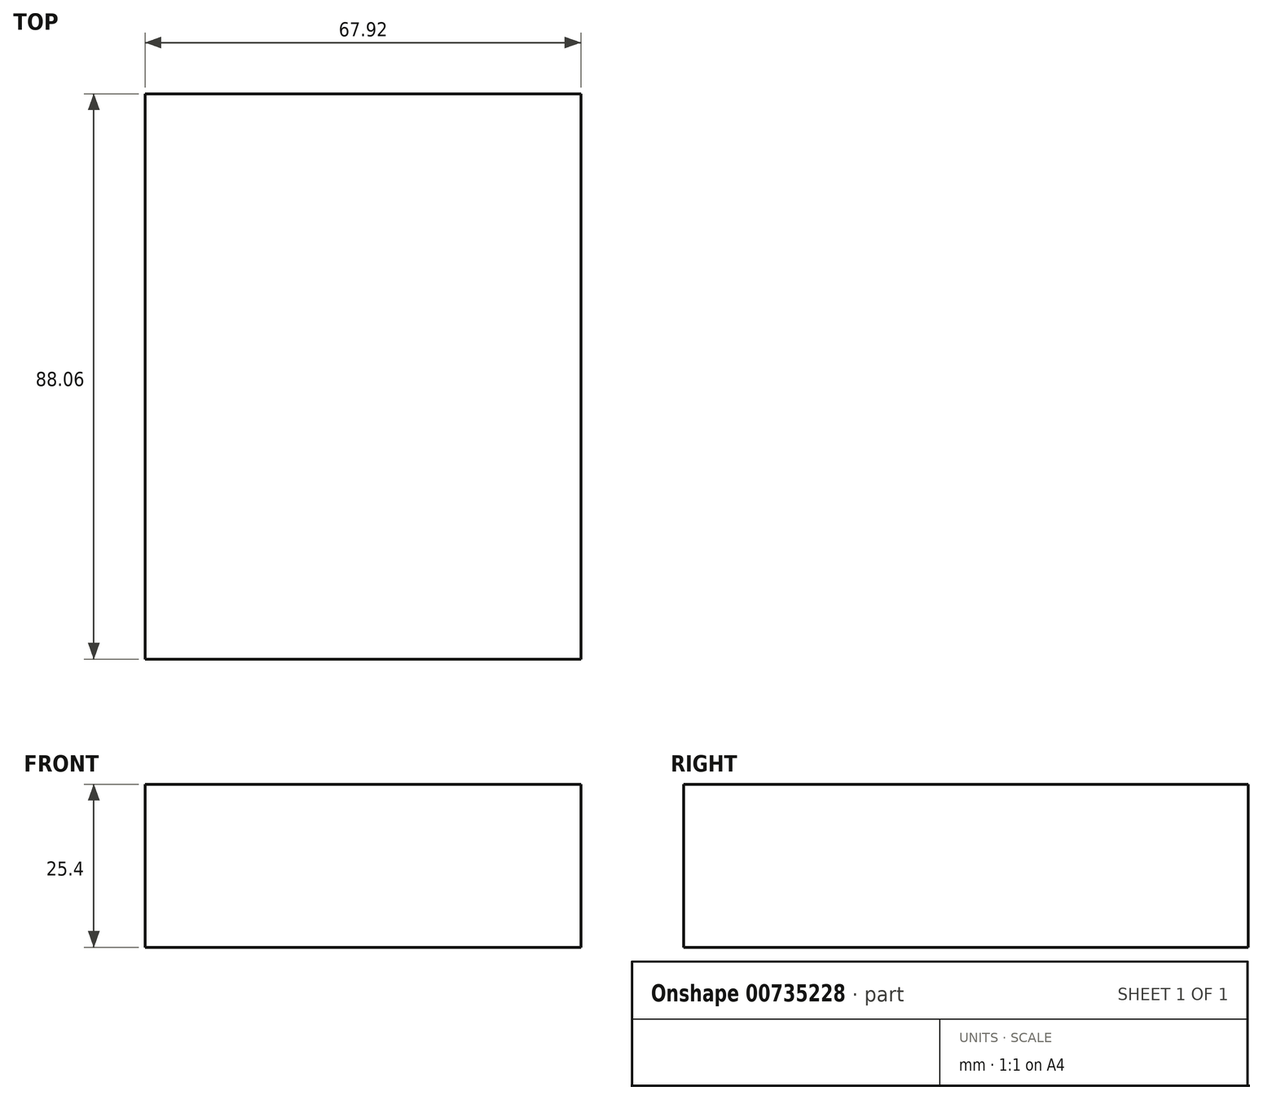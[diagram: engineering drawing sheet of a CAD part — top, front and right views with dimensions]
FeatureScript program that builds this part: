
annotation { "Feature Type Name" : "Feature", "Feature Type Description" : "" }
export const myFeature = defineFeature(function(context is Context, id is Id, definition is map)
    precondition{}
    {
        {
            var Q0;
            Q0=qCreatedBy(makeId("Top.planeOp"),FACE);
            var sketch = newSketch(context, id + "F0", { "sketchPlane" : qUnion([Q0])});
            skLineSegment(sketch, "E0.bottom", {"start": v(33.96, 44.03) * mm, "end": v(-33.96, 44.03) * mm});
            skLineSegment(sketch, "E0.top", {"start": v(33.96, -44.03) * mm, "end": v(-33.96, -44.03) * mm});
            skLineSegment(sketch, "E0.left", {"start": v(33.96, 44.03) * mm, "end": v(33.96, -44.03) * mm});
            skLineSegment(sketch, "E0.right", {"start": v(-33.96, 44.03) * mm, "end": v(-33.96, -44.03) * mm});
            skPoint(sketch, "E0.middle", {"position": v(0, 0) * mm});
            skSolve(sketch);
        }
        {
            var Q0;
            Q0=makeQuery(id+"F0.imprint","IMPRINT",FACE,{"disambiguationData":[TD([[makeQuery(id+"F0.imprint","IMPRINT",EDGE,{"derivedFrom":sQuery(id+"F0.wireOp",EDGE,"E0.bottom")}),1.0]])]});
            var Q1;
            Q1 = qSketchRegion(id + "F0", true);
            extrude(context, id + "F1", {"entities" : qUnion([Q0, Q1]), "depth" : 25.4 * mm, "offsetDistance" : 25.4 * mm});
        }
        {
            var Q0;
            Q0=makeQuery(id+"F0.imprint","IMPRINT",FACE,{"disambiguationData":[TD([[makeQuery(id+"F0.imprint","IMPRINT",EDGE,{"derivedFrom":sQuery(id+"F0.wireOp",EDGE,"E0.bottom")}),1.0]])]});
            extrude(context, id + "F2", {"entities" : qUnion([Q0]), "depth" : 25.4 * mm});
        }
    });
